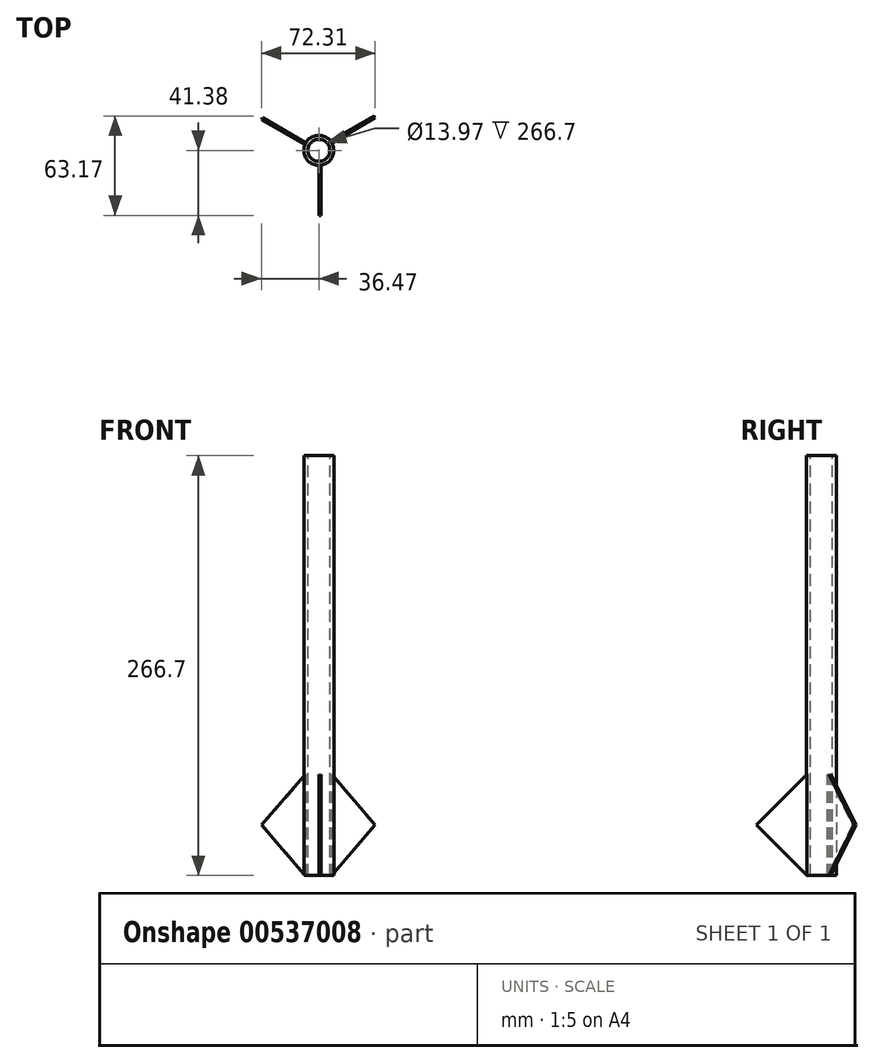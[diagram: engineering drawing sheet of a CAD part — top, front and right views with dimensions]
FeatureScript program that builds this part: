
annotation { "Feature Type Name" : "Feature", "Feature Type Description" : "" }
export const myFeature = defineFeature(function(context is Context, id is Id, definition is map)
    precondition{}
    {
        {
            var Q0;
            Q0=qCreatedBy(makeId("Top.planeOp"),FACE);
            var sketch = newSketch(context, id + "F0", { "sketchPlane" : qUnion([Q0])});
            skCircle(sketch, "E0", {"center": v(0, 0) * mm, "radius": 9.53 * mm});
            skSolve(sketch);
        }
        {
            var Q0;
            Q0=qCreatedBy(makeId("Top.planeOp"),FACE);
            var sketch = newSketch(context, id + "F1", { "sketchPlane" : qUnion([Q0])});
            skCircle(sketch, "E1", {"center": v(0, 0) * mm, "radius": 6.99 * mm});
            skSolve(sketch);
        }
        {
            var Q0;
            Q0=makeQuery(id+"F0.imprint","IMPRINT",FACE,{"disambiguationData":[TD([[makeQuery(id+"F0.imprint","IMPRINT",EDGE,{"derivedFrom":sQuery(id+"F0.wireOp",EDGE,"E0")}),1.0]])]});
            extrude(context, id + "F2", {"entities" : qUnion([Q0]), "depth" : 266.7 * mm, "offsetDistance" : 25.4 * mm});
        }
        {
            var Q0;
            Q0=makeQuery(id+"F1.imprint","IMPRINT",FACE,{"disambiguationData":[TD([[makeQuery(id+"F1.imprint","IMPRINT",EDGE,{"derivedFrom":sQuery(id+"F1.wireOp",EDGE,"E1")}),1.0]])]});
            var Q1;
            Q1=sQuery(id+"F1.wireOp",EDGE,"E1");
            extrude(context, id + "F3", {"entities" : qUnion([Q0]), "operationType" : NewBodyOperationType.REMOVE, "surfaceEntities" : qUnion([Q1]), "oppositeDirection" : true, "depth" : 266.7 * mm, "offsetDistance" : 25.4 * mm, "hasSecondDirection" : true, "secondDirectionOppositeDirection" : false, "secondDirectionDepth" : 266.7 * mm});
        }
        {
            var Q0;
            Q0=qCreatedBy(makeId("Right.planeOp"),FACE);
            var sketch = newSketch(context, id + "F4", { "sketchPlane" : qUnion([Q0])});
            skLineSegment(sketch, "E2", {"start": v(-9.5, 0) * mm, "end": v(-9.5, 64.05) * mm});
            skLineSegment(sketch, "E3", {"start": v(-9.5, 32.02) * mm, "end": v(-41.38, 32.02) * mm});
            skLineSegment(sketch, "E4", {"start": v(-9.5, 64.05) * mm, "end": v(-41.38, 32.02) * mm});
            skLineSegment(sketch, "E5", {"start": v(-41.38, 32.02) * mm, "end": v(-9.5, 0) * mm});
            skSolve(sketch);
        }
        {
            var Q0;
            {var subQ2=sQuery(id+"F4.wireOp",EDGE,"E3");Q0=makeQuery(id+"F4.imprint","IMPRINT",FACE,{"disambiguationData":[TD([[makeQuery(id+"F4.imprint","IMPRINT",EDGE,{"derivedFrom":subQ2}),-1.0]])]});}
            var Q1;
            {var subQ2=sQuery(id+"F4.wireOp",EDGE,"E3");Q1=makeQuery(id+"F4.imprint","IMPRINT",FACE,{"disambiguationData":[TD([[makeQuery(id+"F4.imprint","IMPRINT",EDGE,{"derivedFrom":subQ2}),1.0]])]});}
            extrude(context, id + "F5", {"entities" : qUnion([Q0, Q1]), "depth" : 1.27 * mm, "offsetDistance" : 25.4 * mm});
        }
        {
            var Q0;
            Q0=makeQuery(id+"F5.opExtrude","SWEPT_BODY",BODY,{"disambiguationData":[OSD([sQuery(id+"F4.wireOp",EDGE,"E2"),sQuery(id+"F4.wireOp",EDGE,"E4"),sQuery(id+"F4.wireOp",EDGE,"E5")])]});
            var Q1;
            Q1=makeQuery(id+"F2.opExtrude","SWEPT_FACE",FACE,{"disambiguationData":[OSD([sQuery(id+"F0.wireOp",EDGE,"E0")])]});
            transform(context, id + "F6", {"entities" : qUnion([Q0]), "transformType" : TransformType.ROTATION, "transformAxis" : qUnion([Q1]), "angle" : 120 * degree, "makeCopy" : true});
        }
        {
            var Q0;
            Q0=makeQuery(id+"F6.opPattern","COPY",BODY,{"derivedFrom":makeQuery(id+"F5.opExtrude","SWEPT_BODY",BODY,{"disambiguationData":[OSD([sQuery(id+"F4.wireOp",EDGE,"E2"),sQuery(id+"F4.wireOp",EDGE,"E4"),sQuery(id+"F4.wireOp",EDGE,"E5")])]}),"instanceName":"1"});
            var Q1;
            Q1=makeQuery(id+"F2.opExtrude","SWEPT_FACE",FACE,{"disambiguationData":[OSD([sQuery(id+"F0.wireOp",EDGE,"E0")])]});
            transform(context, id + "F7", {"entities" : qUnion([Q0]), "transformType" : TransformType.ROTATION, "transformAxis" : qUnion([Q1]), "angle" : 120 * degree, "makeCopy" : true});
        }
    });
